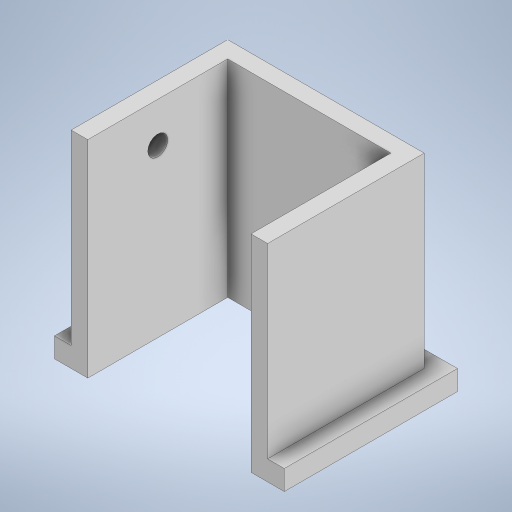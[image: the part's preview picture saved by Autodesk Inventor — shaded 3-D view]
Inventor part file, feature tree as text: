
AUTODESK INVENTOR PART (.ipt)
format: ipt  version: 2023 (Build 270158000, 158)  size: 262,656 bytes
history: native  units: in
note: dims shown in document units (in); Inventor stores cm internally (conversion verified against a paired STEP export)
features: sketch x5, extrude x4
ambient origin geometry x8: Origin, YZ Plane, XZ Plane, XY Plane, X Axis, Y Axis, Z Axis, Center Point
bodies: Solid1 (feature_tree)
feature tree (9):
  extrude  "Extrusion1"  Depth=0.1969in
  extrude  "Extrusion7"  Depth=1.6535in
  extrude  "Extrusion8"  Depth=1.6535in
  sketch  "Sketch9"  dims[d6=2.4409in d7=0.0in d34=0.1969in]
  extrude  "Extrusion9"  Depth=0.1969in
  sketch  "Sketch1"  dims[d0=2.3228in d1=0.1969in]
  sketch  "Sketch7"  dims[d2=0.1969in d3=1.6535in]
  sketch  "Sketch8"  dims[d4=0.1969in d5=1.6535in]
  sketch  "Sketch10"  dims[d35=2.0472in d36=0.1969in d37=2.0472in d38=0.2362in d39=0.0in d40=0.3937in d41=0.1969in d42=0.3937in d43=0.1969in d44=1.3583in d47=0.1969in d48=0.1969in d49=0.1969in d50=0.0in d51=0.8268in d52=1.9685in d53=0.2362in d54=0.1969in d55=0.0in d56=0.5118in d57=0.5118in d11=0.0197in d12=0.0344in d13=0.0197in d14=0.0344in]
